# Revit family: hb_610_612322_0031_e213
name_source: partatom
category: Lighting Fixtures
units: mm (PartAtom-declared; Revit-internal decimal feet)

## family parameters
Cut with Voids When Loaded = No
Host = Face
Light Source = No
Part Type = Normal
Room Calculation Point = No
Round Connector Dimension = Use Diameter
Shared = No

## types (1)
- HB 610 (1 x LED Modul 830, 5600 lm, 3000)
    Apparent Load = 50 VA
    CIE Flux Codes = 45 85 99 100 100
    Color Rendering = 80
    Color Temperature = 3000
    Default Elevation = 1800 mm
    Description = Series: HB 610
Functional pole-top or pole-side mounted luminaire. Housing: die-cast aluminium, powder-coated. One piece multi-layer lens cover. Wide beam light distribution. Universal pole attachment for pole top Ø 42-44 mm, 60-76 mm and wall mounting.  Tilt angle can be adjusted and locked in 5° steps. Exchangeable mains voltage LED. Pre-wired with 500 mm connection cable. Please order reducer adapter for pole clamp D 42 mm separately. 
Colour: anthracite metallic (DB703)
Length: 445 mm
Width: 154 mm
Height: 112 mm
Lamp: LED
System power: 50 W
Rated luminous flux: 5600 lm
Luminous efficiency: 112 lm/W
Control gear: Converter not necessary
Protection class: I
Type of protection: IP 65
    Height = 112 mm
    Lamp = 1 x LED Modul 830
    Lamp Light Flux = 5600 lm
    Lamp count = 1
    Length = 445 mm
    Lifetime = 50000 h
    Luminous efficacy = 112 lm/W
    Manufacturer = RZB
    ModVariant = No
    Model = 612322.0031
    Mounting Place = Floor
    Mounting Type = Freestanding
    Number of Poles = 1
    OnlyDefault = Yes
    Power Factor = 1
    Product Name = HB 610
    Product group = Pole luminaires
    ProductGroupID = 1352
    Protection Class = Protection class I
    Protection Degree = IP 65
    RLX_Detail_Level = 1
    RLX_Emergency_Light_Flux = 0 lm
    RLX_Emergency_Type = 0
    RLX_Emergency_Type_DB = No
    RlxData = <blob elided: 43425 chars, md5=7b4b34ed>
    Socket = socket
    Standby Power = 0 W
    System Light Flux = 5600 lm
    System Power = 50 W
    Type Comments = Product without accessories
    Type Image = 612322.0031.jpg
    URL = http://relux.com
    VarID = ---
    Voltage = 0 V
    Weight = 0.00 kg
    Width = 154 mm

## geometry (parser evidence)
native form markers: Sweep x9
no freeform markers — native parametric forms only
